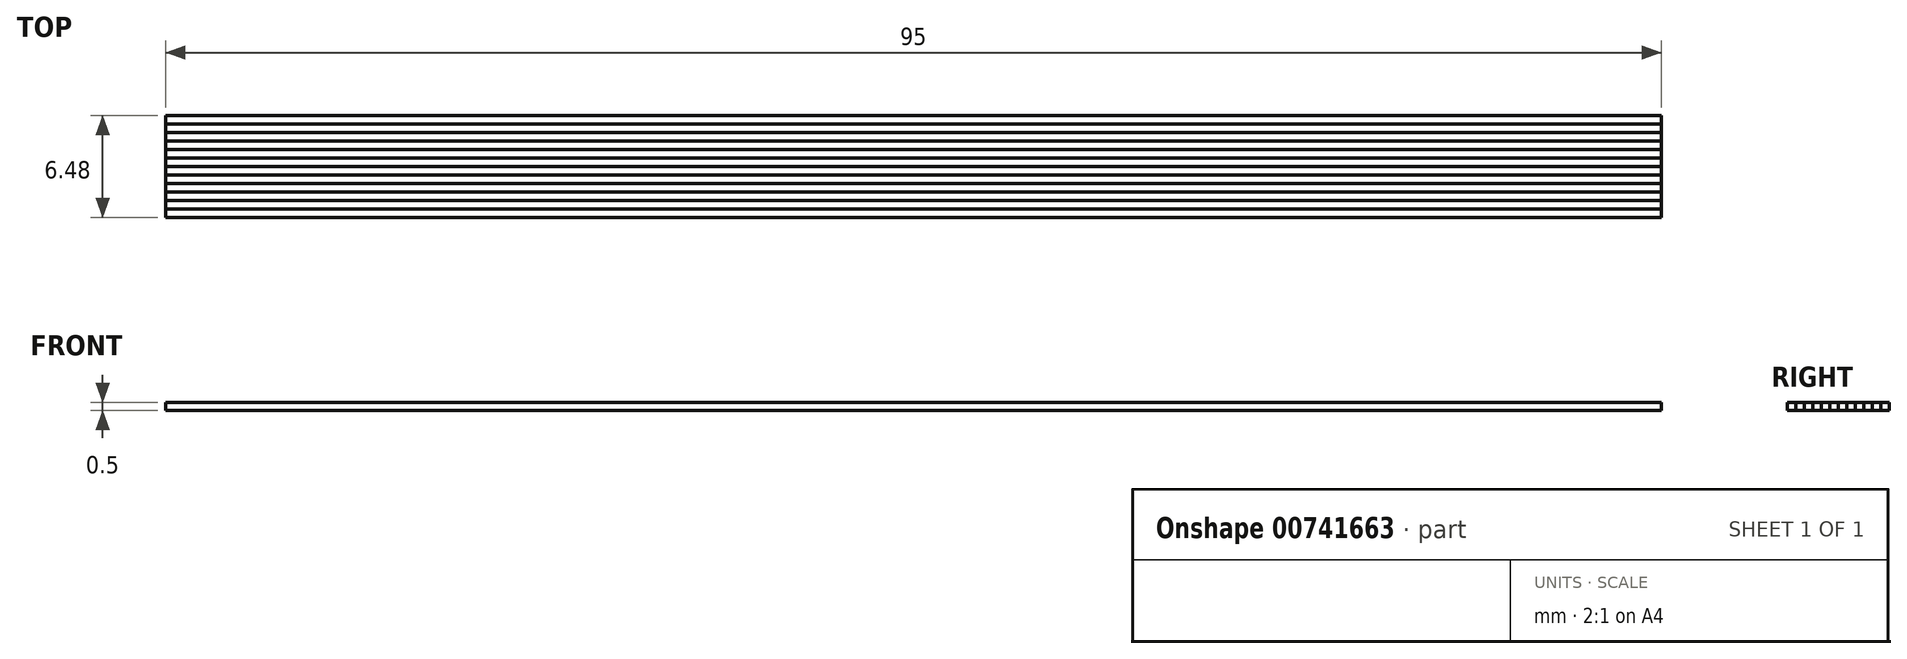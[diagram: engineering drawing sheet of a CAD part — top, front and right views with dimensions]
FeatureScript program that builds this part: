
annotation { "Feature Type Name" : "Feature", "Feature Type Description" : "" }
export const myFeature = defineFeature(function(context is Context, id is Id, definition is map)
    precondition{}
    {
        {
            var Q0;
            Q0=qCreatedBy(makeId("Top.planeOp"),FACE);
            var sketch = newSketch(context, id + "F0", { "sketchPlane" : qUnion([Q0])});
            skLineSegment(sketch, "E0.bottom", {"start": v(47.5, 3.25) * mm, "end": v(-47.5, 3.25) * mm});
            skLineSegment(sketch, "E0.top", {"start": v(47.5, -3.25) * mm, "end": v(-47.5, -3.25) * mm});
            skLineSegment(sketch, "E0.left", {"start": v(47.5, 3.25) * mm, "end": v(47.5, -3.25) * mm});
            skLineSegment(sketch, "E0.right", {"start": v(-47.5, 3.25) * mm, "end": v(-47.5, -3.25) * mm});
            skPoint(sketch, "E0.middle", {"position": v(0, 0) * mm});
            skLineSegment(sketch, "E1", {"start": v(-47.5, 2.71) * mm, "end": v(47.5, 2.7) * mm});
            skLineSegment(sketch, "E2.0.1.0", {"start": v(-47.5, 2.17) * mm, "end": v(47.5, 2.17) * mm});
            skLineSegment(sketch, "E2.0.2.0", {"start": v(-47.5, 1.63) * mm, "end": v(47.5, 1.63) * mm});
            skLineSegment(sketch, "E2.0.3.0", {"start": v(-47.5, 1.09) * mm, "end": v(47.5, 1.1) * mm});
            skLineSegment(sketch, "E2.0.4.0", {"start": v(-47.5, 0.55) * mm, "end": v(47.5, 0.55) * mm});
            skLineSegment(sketch, "E2.0.5.0", {"start": v(-47.5, 0) * mm, "end": v(47.5, 0.01) * mm});
            skLineSegment(sketch, "E2.0.6.0", {"start": v(-47.5, -0.53) * mm, "end": v(47.5, -0.53) * mm});
            skLineSegment(sketch, "E2.0.7.0", {"start": v(-47.5, -1.07) * mm, "end": v(47.5, -1.07) * mm});
            skLineSegment(sketch, "E2.0.8.0", {"start": v(-47.5, -1.61) * mm, "end": v(47.5, -1.6) * mm});
            skLineSegment(sketch, "E2.0.9.0", {"start": v(-47.5, -2.15) * mm, "end": v(47.5, -2.15) * mm});
            skLineSegment(sketch, "E2.0.10.0", {"start": v(-47.5, -2.7) * mm, "end": v(47.5, -2.69) * mm});
            skLineSegment(sketch, "E2.0.11.0", {"start": v(-47.5, -3.23) * mm, "end": v(47.5, -3.23) * mm});
            skLineSegment(sketch, "E2.direction1", {"start": v(-47.5, 2.71) * mm, "end": v(-23.9, 2.71) * mm, "construction": true});
            skLineSegment(sketch, "E2.direction2", {"start": v(-47.5, 2.71) * mm, "end": v(-47.5, 2.17) * mm, "construction": true});
            skSolve(sketch);
        }
        {
            var Q0;
            {var subQ0=sQuery(id+"F0.wireOp",EDGE,"E0.bottom");Q0=makeQuery(id+"F0.imprint","IMPRINT",FACE,{"disambiguationData":[TD([[makeQuery(id+"F0.imprint","IMPRINT",EDGE,{"derivedFrom":subQ0}),1.0]])]});}
            var Q1;
            {var subQ0=sQuery(id+"F0.wireOp",EDGE,"E2.0.1.0");Q1=makeQuery(id+"F0.imprint","IMPRINT",FACE,{"disambiguationData":[TD([[makeQuery(id+"F0.imprint","IMPRINT",EDGE,{"derivedFrom":subQ0}),-1.0]])]});}
            var Q2;
            {var subQ0=sQuery(id+"F0.wireOp",EDGE,"E2.0.3.0");Q2=makeQuery(id+"F0.imprint","IMPRINT",FACE,{"disambiguationData":[TD([[makeQuery(id+"F0.imprint","IMPRINT",EDGE,{"derivedFrom":subQ0}),-1.0]])]});}
            var Q3;
            {var subQ0=sQuery(id+"F0.wireOp",EDGE,"E2.0.5.0");Q3=makeQuery(id+"F0.imprint","IMPRINT",FACE,{"disambiguationData":[TD([[makeQuery(id+"F0.imprint","IMPRINT",EDGE,{"derivedFrom":subQ0}),-1.0]])]});}
            var Q4;
            {var subQ0=sQuery(id+"F0.wireOp",EDGE,"E2.0.7.0");Q4=makeQuery(id+"F0.imprint","IMPRINT",FACE,{"disambiguationData":[TD([[makeQuery(id+"F0.imprint","IMPRINT",EDGE,{"derivedFrom":subQ0}),-1.0]])]});}
            var Q5;
            {var subQ0=sQuery(id+"F0.wireOp",EDGE,"E2.0.9.0");Q5=makeQuery(id+"F0.imprint","IMPRINT",FACE,{"disambiguationData":[TD([[makeQuery(id+"F0.imprint","IMPRINT",EDGE,{"derivedFrom":subQ0}),-1.0]])]});}
            extrude(context, id + "F1", {"entities" : qUnion([Q0, Q1, Q2, Q3, Q4, Q5]), "depth" : 0.5 * mm, "offsetDistance" : 25 * mm});
        }
        {
            var Q0;
            {var subQ0=sQuery(id+"F0.wireOp",EDGE,"E1");Q0=makeQuery(id+"F0.imprint","IMPRINT",FACE,{"disambiguationData":[TD([[makeQuery(id+"F0.imprint","IMPRINT",EDGE,{"derivedFrom":subQ0}),-1.0]])]});}
            var Q1;
            {var subQ0=sQuery(id+"F0.wireOp",EDGE,"E2.0.2.0");Q1=makeQuery(id+"F0.imprint","IMPRINT",FACE,{"disambiguationData":[TD([[makeQuery(id+"F0.imprint","IMPRINT",EDGE,{"derivedFrom":subQ0}),-1.0]])]});}
            var Q2;
            {var subQ0=sQuery(id+"F0.wireOp",EDGE,"E2.0.4.0");Q2=makeQuery(id+"F0.imprint","IMPRINT",FACE,{"disambiguationData":[TD([[makeQuery(id+"F0.imprint","IMPRINT",EDGE,{"derivedFrom":subQ0}),-1.0]])]});}
            var Q3;
            {var subQ0=sQuery(id+"F0.wireOp",EDGE,"E2.0.6.0");Q3=makeQuery(id+"F0.imprint","IMPRINT",FACE,{"disambiguationData":[TD([[makeQuery(id+"F0.imprint","IMPRINT",EDGE,{"derivedFrom":subQ0}),-1.0]])]});}
            var Q4;
            {var subQ0=sQuery(id+"F0.wireOp",EDGE,"E2.0.8.0");Q4=makeQuery(id+"F0.imprint","IMPRINT",FACE,{"disambiguationData":[TD([[makeQuery(id+"F0.imprint","IMPRINT",EDGE,{"derivedFrom":subQ0}),-1.0]])]});}
            var Q5;
            {var subQ0=sQuery(id+"F0.wireOp",EDGE,"E2.0.10.0");Q5=makeQuery(id+"F0.imprint","IMPRINT",FACE,{"disambiguationData":[TD([[makeQuery(id+"F0.imprint","IMPRINT",EDGE,{"derivedFrom":subQ0}),-1.0]])]});}
            extrude(context, id + "F2", {"entities" : qUnion([Q0, Q1, Q2, Q3, Q4, Q5]), "depth" : 0.5 * mm, "offsetDistance" : 25 * mm});
        }
    });
